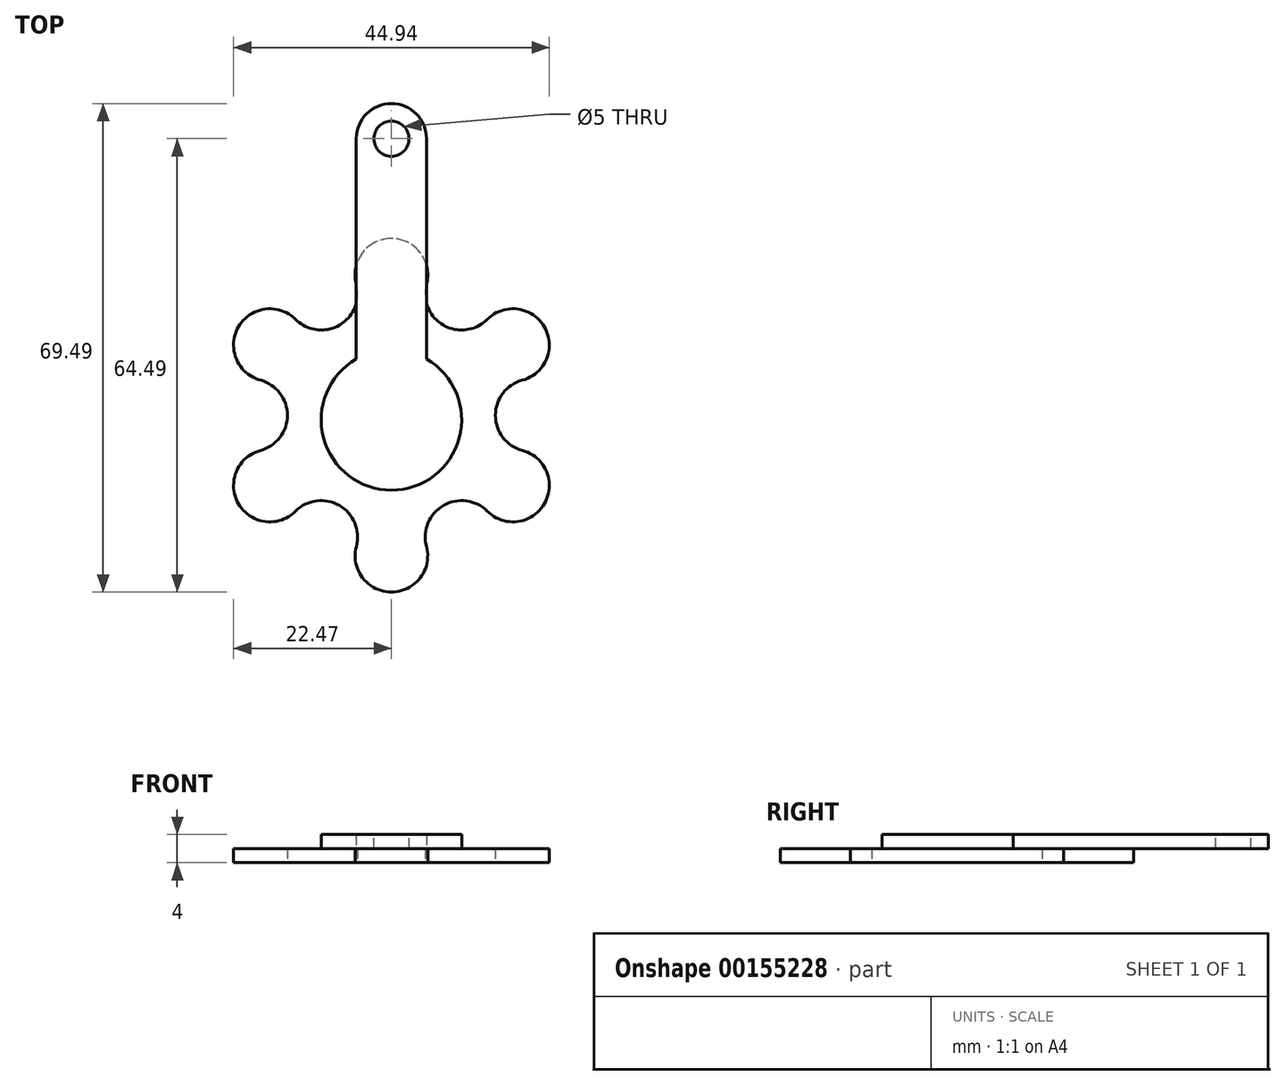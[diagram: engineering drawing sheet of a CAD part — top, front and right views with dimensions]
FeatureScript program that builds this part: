
annotation { "Feature Type Name" : "Feature", "Feature Type Description" : "" }
export const myFeature = defineFeature(function(context is Context, id is Id, definition is map)
    precondition{}
    {
        {
            var Q0;
            Q0=qCreatedBy(makeId("Top.planeOp"),FACE);
            var sketch = newSketch(context, id + "F0", { "sketchPlane" : qUnion([Q0])});
            skArc(sketch, "E0", {"start": v(-13.64, 14.3) * mm, "mid": v(-21.78, 13.23) * mm, "end": v(-18.64, 5.65) * mm});
            skArc(sketch, "E1.1.0", {"start": v(-18.64, -4.34) * mm, "mid": v(-14.8, 0.65) * mm, "end": v(-18.64, 5.65) * mm});
            skArc(sketch, "E1.2.0", {"start": v(-18.64, -4.34) * mm, "mid": v(-21.78, -11.92) * mm, "end": v(-13.64, -12.99) * mm});
            skArc(sketch, "E1.3.0", {"start": v(-5, -17.98) * mm, "mid": v(-7.4, -12.17) * mm, "end": v(-13.64, -12.99) * mm});
            skArc(sketch, "E1.4.0", {"start": v(-5, -17.98) * mm, "mid": v(0, -24.5) * mm, "end": v(5, -17.98) * mm});
            skArc(sketch, "E1.5.0", {"start": v(13.64, -12.99) * mm, "mid": v(7.4, -12.17) * mm, "end": v(5, -17.98) * mm});
            skArc(sketch, "E1.6.0", {"start": v(13.64, -12.99) * mm, "mid": v(21.78, -11.92) * mm, "end": v(18.64, -4.34) * mm});
            skArc(sketch, "E1.7.0", {"start": v(18.64, 5.65) * mm, "mid": v(14.8, 0.65) * mm, "end": v(18.64, -4.34) * mm});
            skArc(sketch, "E1.8.0", {"start": v(18.64, 5.65) * mm, "mid": v(21.78, 13.23) * mm, "end": v(13.64, 14.3) * mm});
            skArc(sketch, "E1.9.0", {"start": v(5, 19.3) * mm, "mid": v(7.4, 13.48) * mm, "end": v(13.64, 14.3) * mm});
            skArc(sketch, "E1.10.0", {"start": v(5, 19.3) * mm, "mid": v(0, 25.8) * mm, "end": v(-5, 19.3) * mm});
            skArc(sketch, "E1.11.0", {"start": v(-13.64, 14.3) * mm, "mid": v(-7.4, 13.48) * mm, "end": v(-5, 19.3) * mm});
            skPoint(sketch, "E1.center", {"position": v(0, 0.65) * mm});
            skSolve(sketch);
        }
        {
            var Q0;
            Q0 = qSketchRegion(id + "F0", true);
            extrude(context, id + "F1", {"entities" : qUnion([Q0]), "depth" : 2 * mm});
        }
        {
            var Q0;
            Q0=makeQuery(id+"F1.opExtrude","CAP_FACE",FACE,{"disambiguationData":[OSD([sQuery(id+"F0.wireOp",EDGE,"E0"),sQuery(id+"F0.wireOp",EDGE,"E1.1.0"),sQuery(id+"F0.wireOp",EDGE,"E1.2.0"),sQuery(id+"F0.wireOp",EDGE,"E1.3.0"),sQuery(id+"F0.wireOp",EDGE,"E1.4.0"),sQuery(id+"F0.wireOp",EDGE,"E1.5.0"),sQuery(id+"F0.wireOp",EDGE,"E1.6.0"),sQuery(id+"F0.wireOp",EDGE,"E1.7.0"),sQuery(id+"F0.wireOp",EDGE,"E1.8.0"),sQuery(id+"F0.wireOp",EDGE,"E1.9.0"),sQuery(id+"F0.wireOp",EDGE,"E1.10.0"),sQuery(id+"F0.wireOp",EDGE,"E1.11.0")])],"isStart":false});
            var sketch = newSketch(context, id + "F2", { "sketchPlane" : qUnion([Q0])});
            skCircle(sketch, "E2", {"center": v(0, 0) * mm, "radius": 10 * mm});
            skSolve(sketch);
        }
        {
            var Q0;
            Q0 = qSketchRegion(id + "F2", true);
            extrude(context, id + "F3", {"entities" : qUnion([Q0]), "operationType" : NewBodyOperationType.ADD, "depth" : 2 * mm});
        }
        {
            var Q0;
            Q0=makeQuery(id+"F3.opExtrude","CAP_FACE",FACE,{"disambiguationData":[OSD([sQuery(id+"F2.wireOp",EDGE,"E2")])],"isStart":false});
            var sketch = newSketch(context, id + "F4", { "sketchPlane" : qUnion([Q0])});
            skCircle(sketch, "E3", {"center": v(0, 40) * mm, "radius": 2.5 * mm});
            skLineSegment(sketch, "E4", {"start": v(0, 0) * mm, "end": v(-5, 0) * mm});
            skLineSegment(sketch, "E5", {"start": v(-5, 0) * mm, "end": v(-5, 40) * mm});
            skArc(sketch, "E6", {"start": v(5, 40) * mm, "mid": v(0, 45) * mm, "end": v(-5, 40) * mm});
            skLineSegment(sketch, "E7", {"start": v(0, 0) * mm, "end": v(5, 0) * mm});
            skLineSegment(sketch, "E8", {"start": v(5, 0) * mm, "end": v(5, 40) * mm});
            skLineSegment(sketch, "E9", {"start": v(0, 0) * mm, "end": v(0, 20.63) * mm});
            skSolve(sketch);
        }
        {
            var Q0;
            Q0 = qSketchRegion(id + "F4", true);
            extrude(context, id + "F5", {"entities" : qUnion([Q0]), "operationType" : NewBodyOperationType.ADD, "oppositeDirection" : true, "depth" : 2 * mm});
        }
    });
